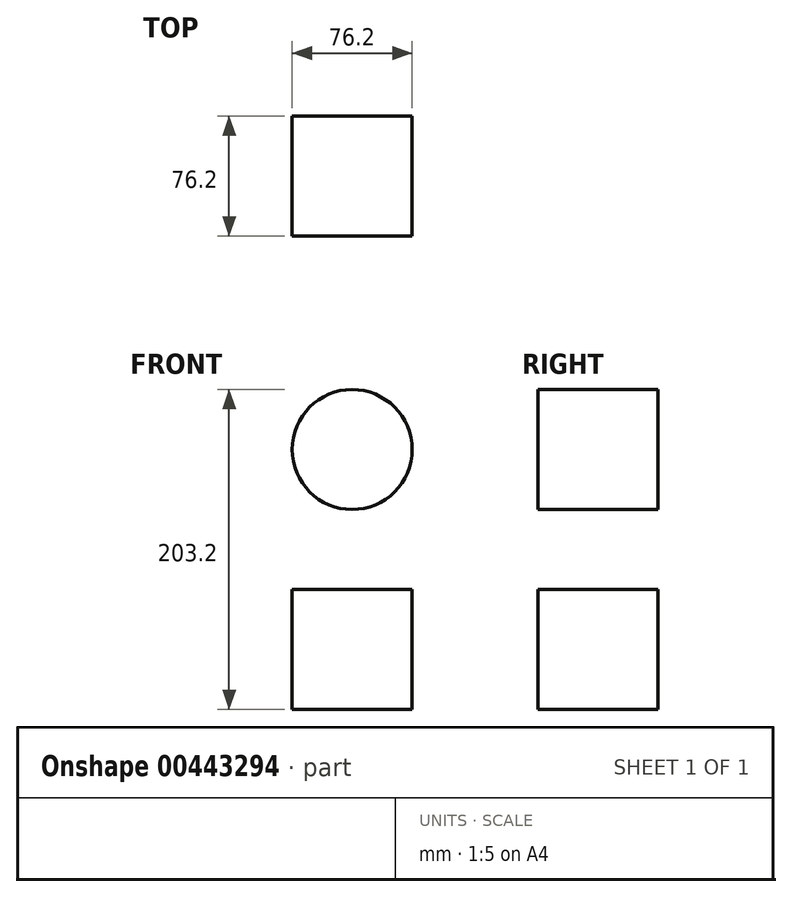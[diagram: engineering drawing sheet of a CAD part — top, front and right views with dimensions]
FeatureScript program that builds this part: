
annotation { "Feature Type Name" : "Feature", "Feature Type Description" : "" }
export const myFeature = defineFeature(function(context is Context, id is Id, definition is map)
    precondition{}
    {
        {
            var Q0;
            Q0=qCreatedBy(makeId("Front.planeOp"),FACE);
            var sketch = newSketch(context, id + "F0", { "sketchPlane" : qUnion([Q0])});
            skLineSegment(sketch, "E0.bottom", {"start": v(38.1, 38.1) * mm, "end": v(-38.1, 38.1) * mm});
            skLineSegment(sketch, "E0.top", {"start": v(38.1, -38.1) * mm, "end": v(-38.1, -38.1) * mm});
            skLineSegment(sketch, "E0.left", {"start": v(38.1, 38.1) * mm, "end": v(38.1, -38.1) * mm});
            skLineSegment(sketch, "E0.right", {"start": v(-38.1, 38.1) * mm, "end": v(-38.1, -38.1) * mm});
            skPoint(sketch, "E0.middle", {"position": v(0, 0) * mm});
            skCircle(sketch, "E1", {"center": v(0, 127) * mm, "radius": 38.1 * mm});
            skSolve(sketch);
        }
        {
            var Q0;
            Q0 = qSketchRegion(id + "F0", true);
            extrude(context, id + "F1", {"entities" : qUnion([Q0]), "depth" : 76.2 * mm});
        }
    });
